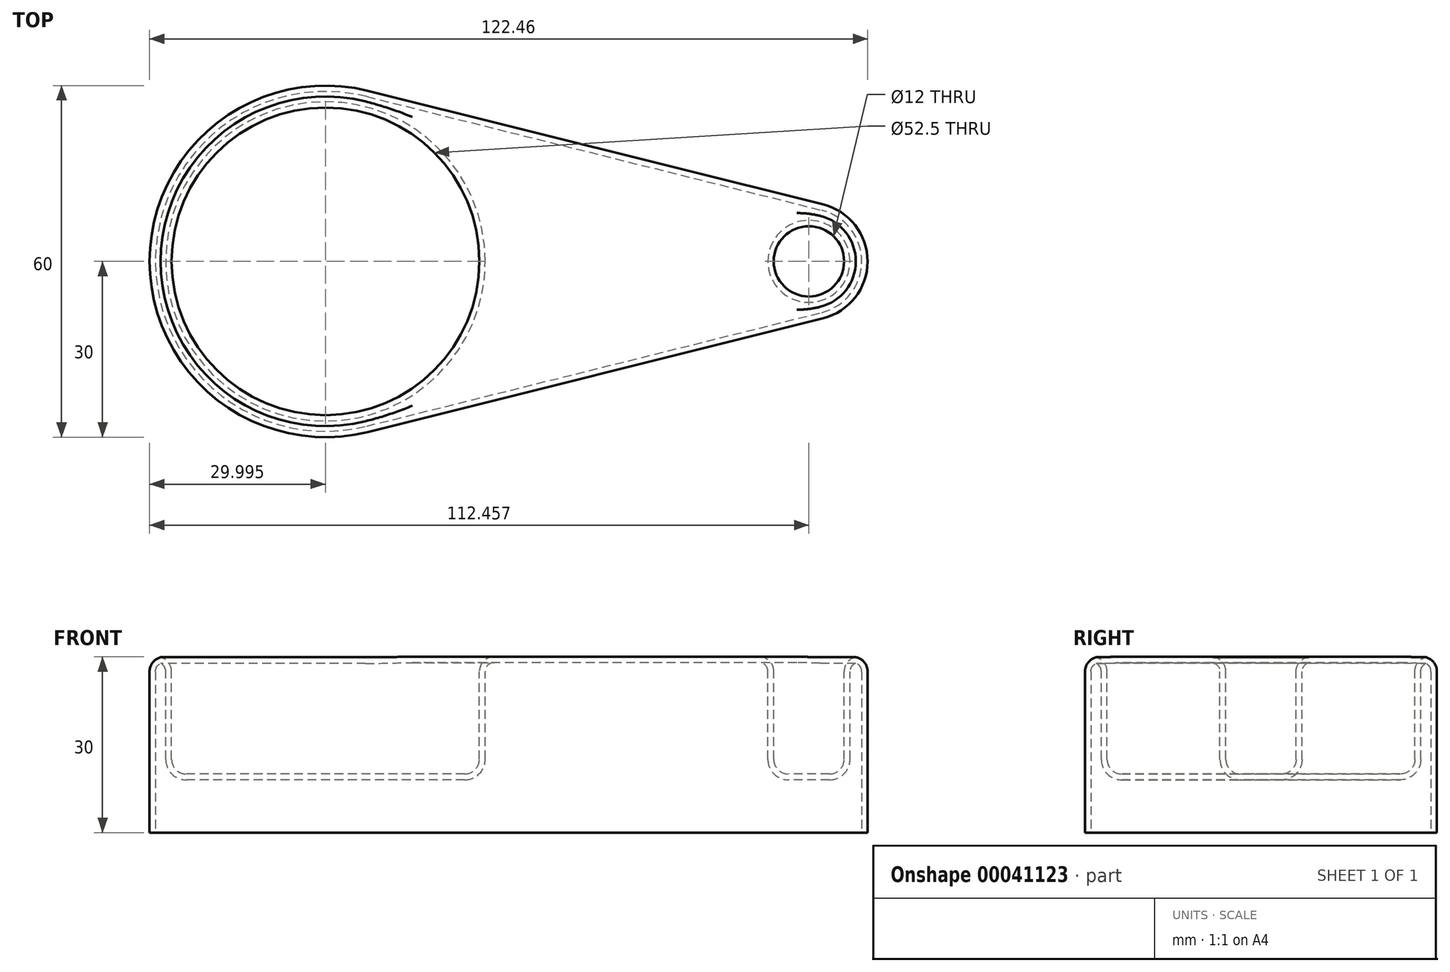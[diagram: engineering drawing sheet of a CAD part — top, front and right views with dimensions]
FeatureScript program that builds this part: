
annotation { "Feature Type Name" : "Feature", "Feature Type Description" : "" }
export const myFeature = defineFeature(function(context is Context, id is Id, definition is map)
    precondition{}
    {
        {
            var Q0;
            Q0=qCreatedBy(makeId("Top.planeOp"),FACE);
            var sketch = newSketch(context, id + "F0", { "sketchPlane" : qUnion([Q0])});
            skCircle(sketch, "E0", {"center": v(-86.26, 0) * mm, "radius": 30 * mm});
            skCircle(sketch, "E1", {"center": v(-3.8, 0) * mm, "radius": 10 * mm});
            skLineSegment(sketch, "E2", {"start": v(-78.99, 29.1) * mm, "end": v(-1.38, 9.7) * mm});
            skLineSegment(sketch, "E3", {"start": v(-78.99, -29.1) * mm, "end": v(-1.38, -9.7) * mm});
            skSolve(sketch);
        }
        {
            var Q0;
            Q0 = qSketchRegion(id + "F0", true);
            extrude(context, id + "F1", {"entities" : qUnion([Q0]), "depth" : 30 * mm});
        }
        {
            var Q0;
            Q0=makeQuery(id+"F1.opExtrude","CAP_FACE",FACE,{"disambiguationData":[OSD([sQuery(id+"F0.wireOp",EDGE,"E0"),sQuery(id+"F0.wireOp",EDGE,"E1"),sQuery(id+"F0.wireOp",EDGE,"E2"),sQuery(id+"F0.wireOp",EDGE,"E3")])],"isStart":false});
            var sketch = newSketch(context, id + "F2", { "sketchPlane" : qUnion([Q0])});
            skCircle(sketch, "E4", {"center": v(-86.26, 0) * mm, "radius": 26.25 * mm});
            skCircle(sketch, "E5", {"center": v(-3.8, 0) * mm, "radius": 6 * mm});
            skSolve(sketch);
        }
        {
            var Q0;
            Q0=makeQuery(id+"F2.imprint","IMPRINT",FACE,{"disambiguationData":[TD([[makeQuery(id+"F2.imprint","IMPRINT",EDGE,{"derivedFrom":sQuery(id+"F2.wireOp",EDGE,"E4")}),1.0]])]});
            var Q1;
            Q1=makeQuery(id+"F2.imprint","IMPRINT",FACE,{"disambiguationData":[TD([[makeQuery(id+"F2.imprint","IMPRINT",EDGE,{"derivedFrom":sQuery(id+"F2.wireOp",EDGE,"E5")}),1.0]])]});
            extrude(context, id + "F3", {"entities" : qUnion([Q0, Q1]), "operationType" : NewBodyOperationType.REMOVE, "oppositeDirection" : true, "depth" : 20 * mm});
        }
        {
            var Q0;
            Q0=makeQuery(id+"F1.opExtrude","CAP_FACE",FACE,{"disambiguationData":[OSD([sQuery(id+"F0.wireOp",EDGE,"E0"),sQuery(id+"F0.wireOp",EDGE,"E1"),sQuery(id+"F0.wireOp",EDGE,"E2"),sQuery(id+"F0.wireOp",EDGE,"E3")])],"isStart":false});
            var Q1;
            Q1=makeQuery(id+"F3.boolean.opBoolean","COPY",EDGE,{"derivedFrom":makeQuery(id+"F3.opExtrude","CAP_EDGE",EDGE,{"disambiguationData":[OSD([sQuery(id+"F2.wireOp",EDGE,"E4")])],"isStart":false})});
            var Q2;
            Q2=makeQuery(id+"F3.boolean.opBoolean","COPY",EDGE,{"derivedFrom":makeQuery(id+"F3.opExtrude","CAP_EDGE",EDGE,{"disambiguationData":[OSD([sQuery(id+"F2.wireOp",EDGE,"E5")])],"isStart":false})});
            fillet(context, id + "F4", {"entities" : qUnion([Q0, Q1, Q2]), "radius" : 2.5 * mm, "tangentPropagation" : true, "allowEdgeOverflow" : false});
        }
        {
            var Q0;
            Q0=makeQuery(id+"F1.opExtrude","CAP_FACE",FACE,{"disambiguationData":[OSD([sQuery(id+"F0.wireOp",EDGE,"E0"),sQuery(id+"F0.wireOp",EDGE,"E1"),sQuery(id+"F0.wireOp",EDGE,"E2"),sQuery(id+"F0.wireOp",EDGE,"E3")])],"isStart":true});
            shell(context, id + "F5", {"entities" : qUnion([Q0]), "thickness" : 1 * mm});
        }
    });
